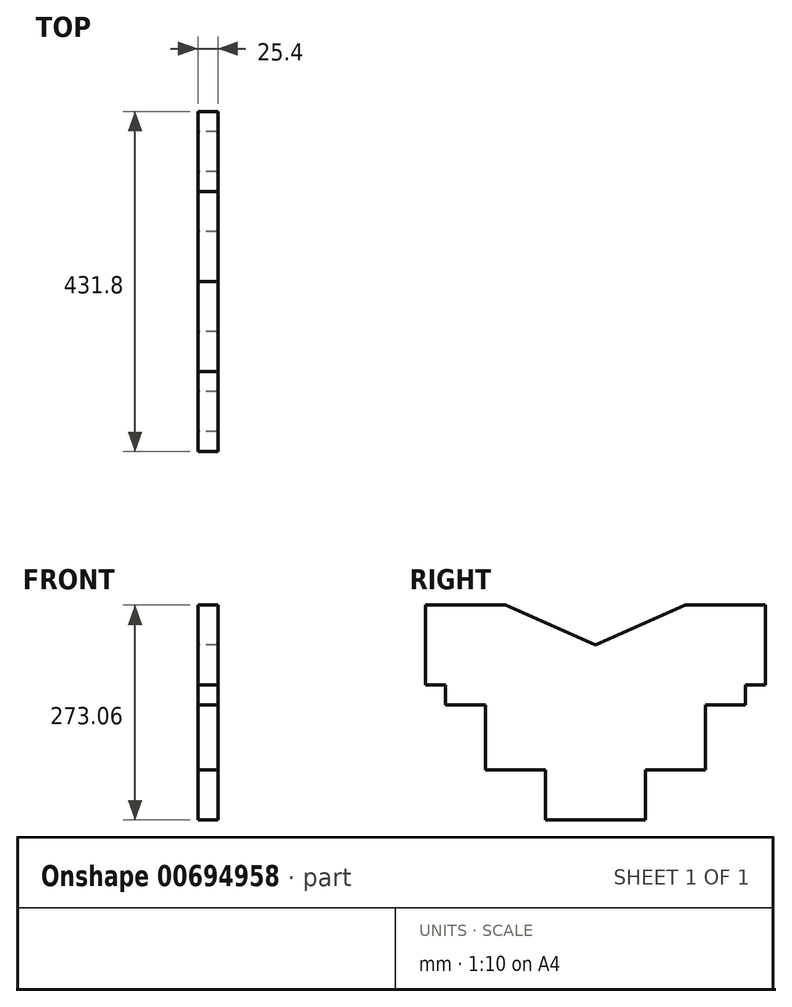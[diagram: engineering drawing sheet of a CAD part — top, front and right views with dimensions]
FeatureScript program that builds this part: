
annotation { "Feature Type Name" : "Feature", "Feature Type Description" : "" }
export const myFeature = defineFeature(function(context is Context, id is Id, definition is map)
    precondition{}
    {
        {
            var Q0;
            Q0=qCreatedBy(makeId("Right.planeOp"),FACE);
            var sketch = newSketch(context, id + "F0", { "sketchPlane" : qUnion([Q0])});
            skLineSegment(sketch, "E0.bottom", {"start": v(-215.9, 136.53) * mm, "end": v(-114.3, 136.53) * mm});
            skLineSegment(sketch, "E0.top", {"start": v(-63.5, -136.53) * mm, "end": v(63.5, -136.53) * mm});
            skLineSegment(sketch, "E0.left", {"start": v(-215.9, 136.53) * mm, "end": v(-215.9, 34.92) * mm});
            skLineSegment(sketch, "E0.right", {"start": v(215.9, 136.53) * mm, "end": v(215.9, 34.92) * mm});
            skPoint(sketch, "E0.middle", {"position": v(0, 0) * mm});
            skLineSegment(sketch, "E1", {"start": v(0, 242.9) * mm, "end": v(0, -229.37) * mm, "construction": true});
            skLineSegment(sketch, "E2.bottom", {"start": v(-63.5, -73.03) * mm, "end": v(-139.7, -73.03) * mm});
            skLineSegment(sketch, "E2.left", {"start": v(-63.5, -73.03) * mm, "end": v(-63.5, -136.52) * mm});
            skLineSegment(sketch, "E3.bottom", {"start": v(-139.7, 9.53) * mm, "end": v(-190.5, 9.53) * mm});
            skLineSegment(sketch, "E3.left", {"start": v(-139.7, 9.53) * mm, "end": v(-139.7, -73.03) * mm});
            skPoint(sketch, "E4.orphan", {"position": v(-215.9, -136.53) * mm});
            skLineSegment(sketch, "E5.0", {"start": v(-215.9, 34.92) * mm, "end": v(-190.5, 34.92) * mm});
            skLineSegment(sketch, "E6.trimOffspring", {"start": v(-190.5, 34.92) * mm, "end": v(-190.5, 9.53) * mm});
            skPoint(sketch, "E7.MirrorP", {"position": v(215.9, -136.53) * mm});
            skLineSegment(sketch, "E8.MirrorCS", {"start": v(139.7, 9.53) * mm, "end": v(139.7, -73.02) * mm});
            skLineSegment(sketch, "E9.MirrorCS", {"start": v(215.9, 34.92) * mm, "end": v(190.5, 34.92) * mm});
            skLineSegment(sketch, "E10.MirrorCS", {"start": v(190.5, 34.92) * mm, "end": v(190.5, 9.53) * mm});
            skLineSegment(sketch, "E11.MirrorCS", {"start": v(139.7, 9.53) * mm, "end": v(190.5, 9.53) * mm});
            skLineSegment(sketch, "E12.MirrorCS", {"start": v(63.5, -73.02) * mm, "end": v(63.5, -136.52) * mm});
            skLineSegment(sketch, "E13.MirrorCS", {"start": v(63.5, -73.03) * mm, "end": v(139.7, -73.03) * mm});
            skLineSegment(sketch, "E14.0", {"start": v(-114.3, 242.9) * mm, "end": v(-114.3, -229.37) * mm, "construction": true});
            skLineSegment(sketch, "E15.0", {"start": v(-215.9, 85.72) * mm, "end": v(215.9, 85.72) * mm, "construction": true});
            skLineSegment(sketch, "E16", {"start": v(-114.3, 136.53) * mm, "end": v(0, 85.72) * mm});
            skLineSegment(sketch, "E17.MirrorCS", {"start": v(114.3, 136.53) * mm, "end": v(0, 85.72) * mm});
            skLineSegment(sketch, "E18.trimOffspring", {"start": v(114.3, 136.53) * mm, "end": v(215.9, 136.53) * mm});
            skSolve(sketch);
        }
        {
            var Q0;
            Q0 = qSketchRegion(id + "F0", true);
            extrude(context, id + "F1", {"entities" : qUnion([Q0]), "depth" : 25.4 * mm, "offsetDistance" : 25.4 * mm});
        }
    });
